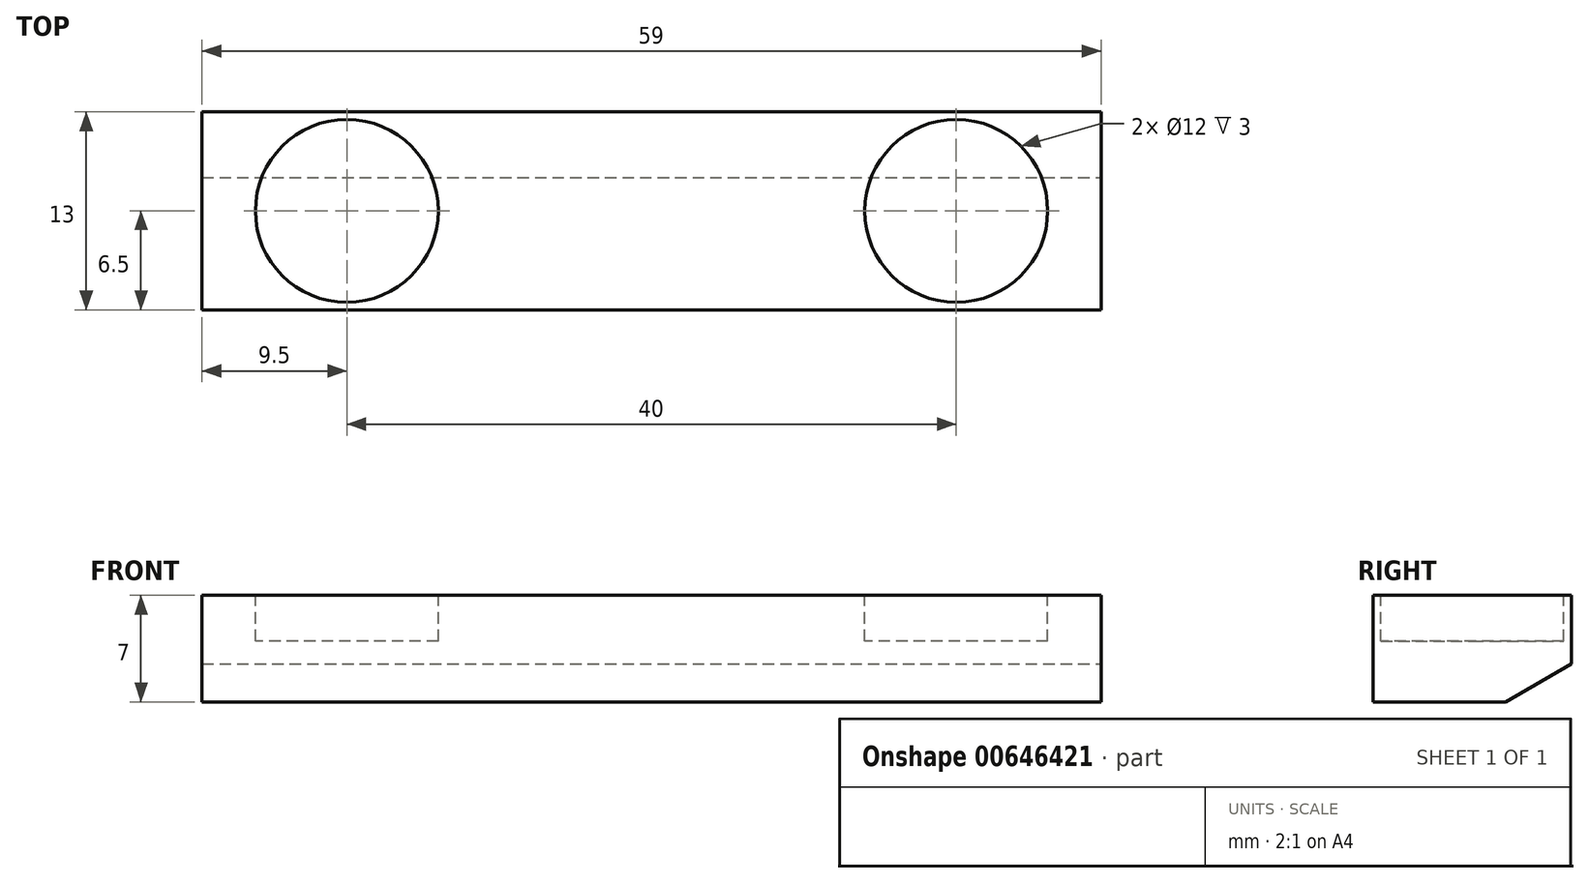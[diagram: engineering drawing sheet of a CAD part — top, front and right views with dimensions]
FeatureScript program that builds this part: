
annotation { "Feature Type Name" : "Feature", "Feature Type Description" : "" }
export const myFeature = defineFeature(function(context is Context, id is Id, definition is map)
    precondition{}
    {
        {
            var Q0;
            Q0=qCreatedBy(makeId("Top.planeOp"),FACE);
            var sketch = newSketch(context, id + "F0", { "sketchPlane" : qUnion([Q0])});
            skLineSegment(sketch, "E0.bottom", {"start": v(29.5, 6.5) * mm, "end": v(-29.5, 6.5) * mm});
            skLineSegment(sketch, "E0.top", {"start": v(29.5, -6.5) * mm, "end": v(-29.5, -6.5) * mm});
            skLineSegment(sketch, "E0.left", {"start": v(29.5, 6.5) * mm, "end": v(29.5, -6.5) * mm});
            skLineSegment(sketch, "E0.right", {"start": v(-29.5, 6.5) * mm, "end": v(-29.5, -6.5) * mm});
            skPoint(sketch, "E0.middle", {"position": v(0, 0) * mm});
            skSolve(sketch);
        }
        {
            var Q0;
            Q0=makeQuery(id+"F0.imprint","IMPRINT",FACE,{"disambiguationData":[TD([[makeQuery(id+"F0.imprint","IMPRINT",EDGE,{"derivedFrom":sQuery(id+"F0.wireOp",EDGE,"E0.bottom")}),1.0]])]});
            extrude(context, id + "F1", {"entities" : qUnion([Q0]), "depth" : 7 * mm, "offsetDistance" : 25 * mm});
        }
        {
            var Q0;
            Q0=makeQuery(id+"F1.opExtrude","CAP_FACE",FACE,{"disambiguationData":[OSD([sQuery(id+"F0.wireOp",EDGE,"E0.bottom"),sQuery(id+"F0.wireOp",EDGE,"E0.top"),sQuery(id+"F0.wireOp",EDGE,"E0.left"),sQuery(id+"F0.wireOp",EDGE,"E0.right")])],"isStart":false});
            var sketch = newSketch(context, id + "F2", { "sketchPlane" : qUnion([Q0])});
            skLineSegment(sketch, "E1", {"start": v(0, 0) * mm, "end": v(20, 0) * mm, "construction": true});
            skLineSegment(sketch, "E2", {"start": v(0, 0) * mm, "end": v(-20, 0) * mm, "construction": true});
            skCircle(sketch, "E3", {"center": v(-20, 0) * mm, "radius": 6 * mm});
            skCircle(sketch, "E4", {"center": v(20, 0) * mm, "radius": 6 * mm});
            skSolve(sketch);
        }
        {
            var Q0;
            Q0=makeQuery(id+"F2.imprint","IMPRINT",FACE,{"disambiguationData":[TD([[makeQuery(id+"F2.imprint","IMPRINT",EDGE,{"derivedFrom":sQuery(id+"F2.wireOp",EDGE,"E3")}),1.0]])]});
            var Q1;
            Q1=makeQuery(id+"F2.imprint","IMPRINT",FACE,{"disambiguationData":[TD([[makeQuery(id+"F2.imprint","IMPRINT",EDGE,{"derivedFrom":sQuery(id+"F2.wireOp",EDGE,"E4")}),1.0]])]});
            extrude(context, id + "F3", {"entities" : qUnion([Q0, Q1]), "operationType" : NewBodyOperationType.REMOVE, "oppositeDirection" : true, "depth" : 3 * mm, "offsetDistance" : 25 * mm});
        }
        {
            var Q0;
            Q0=makeQuery(id+"F1.opExtrude","SWEPT_FACE",FACE,{"disambiguationData":[OSD([sQuery(id+"F0.wireOp",EDGE,"E0.left")])]});
            var sketch = newSketch(context, id + "F4", { "sketchPlane" : qUnion([Q0])});
            skLineSegment(sketch, "E5", {"start": v(6.5, 0) * mm, "end": v(2.2, 0) * mm});
            skLineSegment(sketch, "E6", {"start": v(2.2, 0) * mm, "end": v(6.5, 2.49) * mm});
            skSolve(sketch);
        }
        {
            var Q0;
            {var subQ0=sQuery(id+"F4.wireOp",EDGE,"E5");Q0=makeQuery(id+"F4.imprint","IMPRINT",FACE,{"disambiguationData":[TD([[makeQuery(id+"F4.imprint","IMPRINT",EDGE,{"derivedFrom":subQ0}),-1.0]])]});}
            extrude(context, id + "F5", {"entities" : qUnion([Q0]), "operationType" : NewBodyOperationType.REMOVE, "oppositeDirection" : true, "depth" : 70 * mm, "offsetDistance" : 25 * mm});
        }
    });
